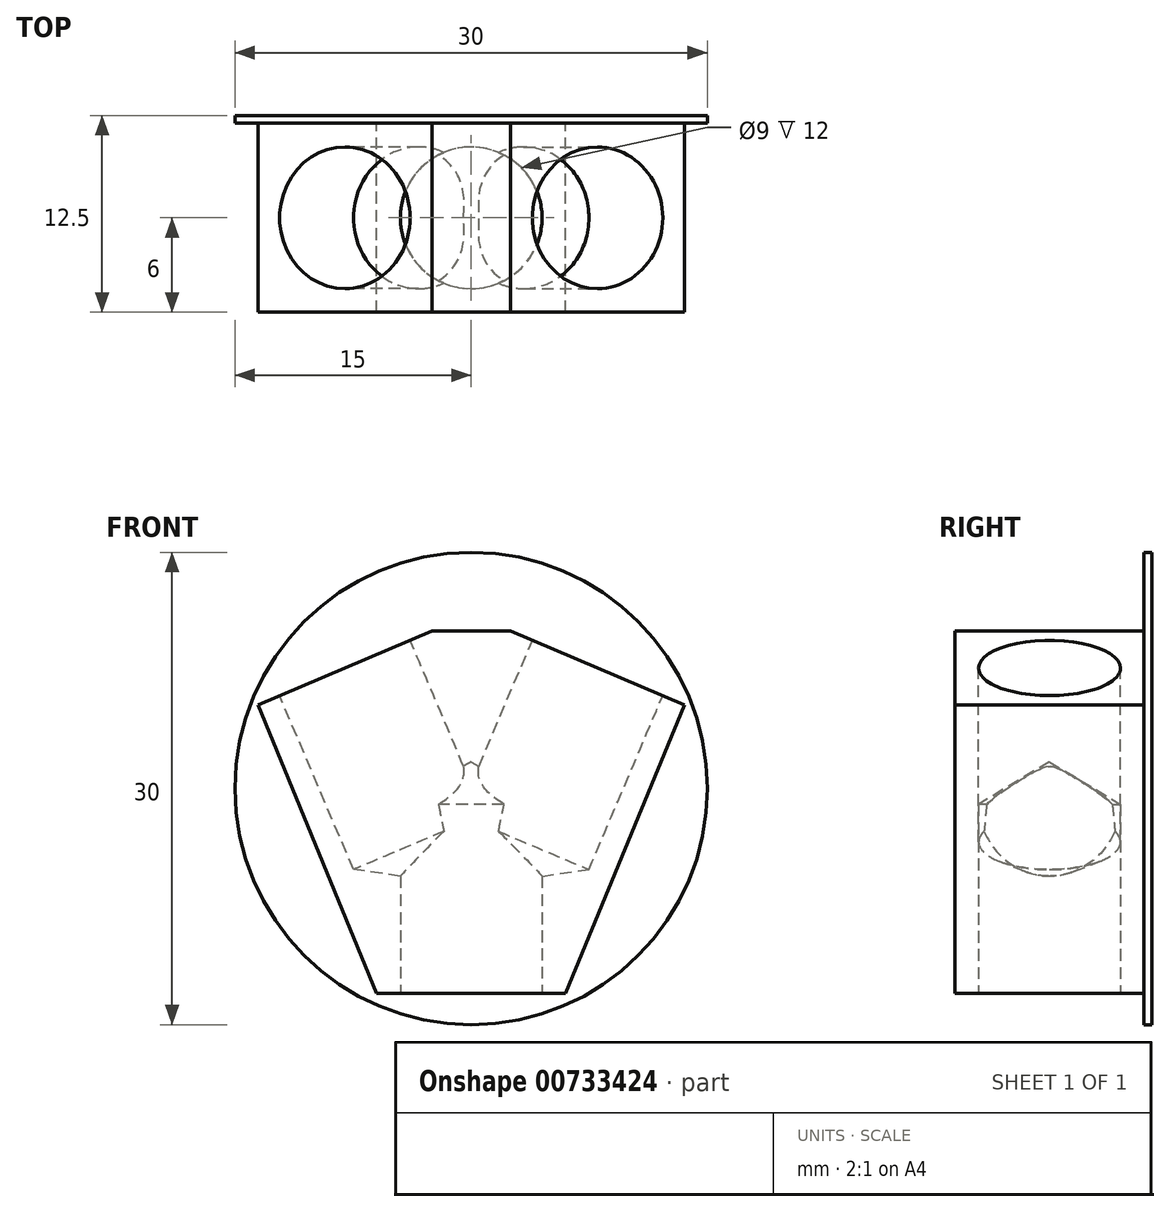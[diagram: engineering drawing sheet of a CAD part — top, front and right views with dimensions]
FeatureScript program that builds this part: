
annotation { "Feature Type Name" : "Feature", "Feature Type Description" : "" }
export const myFeature = defineFeature(function(context is Context, id is Id, definition is map)
    precondition{}
    {
        {
            var Q0;
            Q0=qCreatedBy(makeId("Front.planeOp"),FACE);
            var sketch = newSketch(context, id + "F0", { "sketchPlane" : qUnion([Q0])});
            skLineSegment(sketch, "E0", {"start": v(0, 23) * mm, "end": v(2.5, 23) * mm});
            skLineSegment(sketch, "E1", {"start": v(2.5, 23) * mm, "end": v(13.55, 18.31) * mm});
            skLineSegment(sketch, "E2", {"start": v(13.55, 18.31) * mm, "end": v(6, 0) * mm});
            skLineSegment(sketch, "E3", {"start": v(6, 0) * mm, "end": v(0, 0) * mm});
            skLineSegment(sketch, "E4", {"start": v(0, 0) * mm, "end": v(0, 23) * mm, "construction": true});
            skLineSegment(sketch, "E5.MirrorCS", {"start": v(-6, 0) * mm, "end": v(0, 0) * mm});
            skLineSegment(sketch, "E6.MirrorCS", {"start": v(-2.5, 23) * mm, "end": v(-13.55, 18.31) * mm});
            skLineSegment(sketch, "E7.MirrorCS", {"start": v(0, 23) * mm, "end": v(-2.5, 23) * mm});
            skLineSegment(sketch, "E8.MirrorCS", {"start": v(-13.55, 18.31) * mm, "end": v(-6, 0) * mm});
            skSolve(sketch);
        }
        {
            var Q0;
            Q0 = qSketchRegion(id + "F0", true);
            extrude(context, id + "F1", {"entities" : qUnion([Q0]), "depth" : 12 * mm, "offsetDistance" : 25 * mm});
        }
        {
            var Q0;
            Q0=makeQuery(id+"F1.opExtrude","SWEPT_FACE",FACE,{"disambiguationData":[OSD([sQuery(id+"F0.wireOp",EDGE,"E3"),sQuery(id+"F0.wireOp",EDGE,"E5.MirrorCS")])]});
            var sketch = newSketch(context, id + "F2", { "sketchPlane" : qUnion([Q0])});
            skPoint(sketch, "E9", {"position": v(0, 6) * mm});
            skLineSegment(sketch, "E10", {"start": v(0, 12) * mm, "end": v(0, 0) * mm, "construction": true});
            skSolve(sketch);
        }
        {
            var Q0;
            Q0=sQuery(id+"F2.wireOp",VERTEX,"E9");
            var Q1;
            Q1=makeQuery(id+"F1.opExtrude","SWEPT_BODY",BODY,{"disambiguationData":[OSD([sQuery(id+"F0.wireOp",EDGE,"E0"),sQuery(id+"F0.wireOp",EDGE,"E1"),sQuery(id+"F0.wireOp",EDGE,"E2"),sQuery(id+"F0.wireOp",EDGE,"E3"),sQuery(id+"F0.wireOp",EDGE,"E5.MirrorCS"),sQuery(id+"F0.wireOp",EDGE,"E6.MirrorCS"),sQuery(id+"F0.wireOp",EDGE,"E7.MirrorCS"),sQuery(id+"F0.wireOp",EDGE,"E8.MirrorCS")])]});
            hole(context, id + "F3", {"style" : HoleStyle.SIMPLE, "endStyle" : HoleEndStyle.BLIND, "standardTappedOrClearance" : lookupTablePath({ "standard" : "ISO", "engagement" : "75%", "pitch" : "1 mm", "size" : "M10", "type" : "Tapped" }), "standardBlindInLast" : lookupTablePath({ "standard" : "ISO", "engagement" : "75%", "pitch" : "1 mm", "size" : "M10", "type" : "Tapped" }), "holeDiameter" : 9 * mm, "majorDiameter" : 10 * mm, "showTappedDepth" : true, "holeDepth" : 12 * mm, "isTappedThrough" : true, "tappedDepth" : 12 * mm, "tapClearance" : 0, "startFromSketch" : true, "locations" : qUnion([Q0]), "scope" : qUnion([Q1])});
        }
        {
            var Q0;
            Q0=makeQuery(id+"F1.opExtrude","SWEPT_FACE",FACE,{"disambiguationData":[OSD([sQuery(id+"F0.wireOp",EDGE,"E1")])]});
            var sketch = newSketch(context, id + "F4", { "sketchPlane" : qUnion([Q0])});
            skLineSegment(sketch, "E11", {"start": v(-0.69, 0) * mm, "end": v(-0.69, -12) * mm, "construction": true});
            skPoint(sketch, "E12", {"position": v(-0.69, -6) * mm});
            skSolve(sketch);
        }
        {
            var Q0;
            Q0=sQuery(id+"F4.wireOp",VERTEX,"E12");
            var Q1;
            Q1=makeQuery(id+"F1.opExtrude","SWEPT_BODY",BODY,{"disambiguationData":[OSD([sQuery(id+"F0.wireOp",EDGE,"E0"),sQuery(id+"F0.wireOp",EDGE,"E1"),sQuery(id+"F0.wireOp",EDGE,"E2"),sQuery(id+"F0.wireOp",EDGE,"E3"),sQuery(id+"F0.wireOp",EDGE,"E5.MirrorCS"),sQuery(id+"F0.wireOp",EDGE,"E6.MirrorCS"),sQuery(id+"F0.wireOp",EDGE,"E7.MirrorCS"),sQuery(id+"F0.wireOp",EDGE,"E8.MirrorCS")])]});
            hole(context, id + "F5", {"style" : HoleStyle.SIMPLE, "endStyle" : HoleEndStyle.BLIND, "standardTappedOrClearance" : lookupTablePath({ "standard" : "ISO", "engagement" : "75%", "pitch" : "1 mm", "size" : "M10", "type" : "Tapped" }), "standardBlindInLast" : lookupTablePath({ "standard" : "ISO", "engagement" : "75%", "pitch" : "1 mm", "size" : "M10", "type" : "Tapped" }), "holeDiameter" : 9 * mm, "majorDiameter" : 10 * mm, "showTappedDepth" : true, "holeDepth" : 12 * mm, "isTappedThrough" : true, "tappedDepth" : 12 * mm, "tapClearance" : 0, "startFromSketch" : true, "locations" : qUnion([Q0]), "scope" : qUnion([Q1])});
        }
        {
            var Q0;
            Q0=makeQuery(id+"F1.opExtrude","SWEPT_FACE",FACE,{"disambiguationData":[OSD([sQuery(id+"F0.wireOp",EDGE,"E6.MirrorCS")])]});
            var sketch = newSketch(context, id + "F6", { "sketchPlane" : qUnion([Q0])});
            skLineSegment(sketch, "E13", {"start": v(0.69, 0) * mm, "end": v(0.69, -12) * mm, "construction": true});
            skPoint(sketch, "E14", {"position": v(0.69, -6) * mm});
            skSolve(sketch);
        }
        {
            var Q0;
            Q0=sQuery(id+"F6.wireOp",VERTEX,"E14");
            var Q1;
            Q1=makeQuery(id+"F1.opExtrude","SWEPT_BODY",BODY,{"disambiguationData":[OSD([sQuery(id+"F0.wireOp",EDGE,"E0"),sQuery(id+"F0.wireOp",EDGE,"E1"),sQuery(id+"F0.wireOp",EDGE,"E2"),sQuery(id+"F0.wireOp",EDGE,"E3"),sQuery(id+"F0.wireOp",EDGE,"E5.MirrorCS"),sQuery(id+"F0.wireOp",EDGE,"E6.MirrorCS"),sQuery(id+"F0.wireOp",EDGE,"E7.MirrorCS"),sQuery(id+"F0.wireOp",EDGE,"E8.MirrorCS")])]});
            hole(context, id + "F7", {"style" : HoleStyle.SIMPLE, "endStyle" : HoleEndStyle.BLIND, "standardTappedOrClearance" : lookupTablePath({ "standard" : "ISO", "engagement" : "75%", "pitch" : "1 mm", "size" : "M10", "type" : "Tapped" }), "standardBlindInLast" : lookupTablePath({ "standard" : "ISO", "engagement" : "75%", "pitch" : "1 mm", "size" : "M10", "type" : "Tapped" }), "holeDiameter" : 9 * mm, "majorDiameter" : 10 * mm, "showTappedDepth" : true, "holeDepth" : 12 * mm, "isTappedThrough" : true, "tappedDepth" : 12 * mm, "tapClearance" : 0, "startFromSketch" : true, "locations" : qUnion([Q0]), "scope" : qUnion([Q1])});
        }
        {
            var Q0;
            Q0=makeQuery(id+"F1.opExtrude","CAP_FACE",FACE,{"disambiguationData":[OSD([sQuery(id+"F0.wireOp",EDGE,"E0"),sQuery(id+"F0.wireOp",EDGE,"E1"),sQuery(id+"F0.wireOp",EDGE,"E2"),sQuery(id+"F0.wireOp",EDGE,"E3"),sQuery(id+"F0.wireOp",EDGE,"E5.MirrorCS"),sQuery(id+"F0.wireOp",EDGE,"E6.MirrorCS"),sQuery(id+"F0.wireOp",EDGE,"E7.MirrorCS"),sQuery(id+"F0.wireOp",EDGE,"E8.MirrorCS")])],"isStart":true});
            var sketch = newSketch(context, id + "F8", { "sketchPlane" : qUnion([Q0])});
            skCircle(sketch, "E15", {"center": v(0, 13) * mm, "radius": 15 * mm});
            skSolve(sketch);
        }
        {
            var Q0;
            Q0 = qSketchRegion(id + "F8", true);
            extrude(context, id + "F9", {"entities" : qUnion([Q0]), "operationType" : NewBodyOperationType.ADD, "depth" : .5 * mm, "offsetDistance" : 25 * mm});
        }
    });
